# Revit family: Sanitary_Showers_Mincey-Marble_Mincey-Hinged-Door
name_source: partatom
category: Doors
units: mm (PartAtom-declared; Revit-internal decimal feet)

## family parameters
Always vertical = Yes
Cut with Voids When Loaded = No
OmniClass Number = 23.45.05.14.11.24
OmniClass Title = Shower/Bath Screens, Curtains
Room Calculation Point = No
Shared = No
Work Plane-Based = No

## types (9) — shared parameters
Default Elevation = 0"
Description = Frameless Swing
Door Width Note = Available custom sizes. Please, contact the manufacturer.
Glass Material = Mincey Marble Manufacturing - Glass - Clear
Glass Material Note = Available glass type: Clear, Frosted
Height = 96"
Height Note = Available custom sizes. Please, contact the manufacturer.
Hinged Panel Height = 74 9/16"
Hinged Panel Width = 28"
Manufacturer = Mincey Marble Manufacturing
Product Documentation Link = https://minceymarble.com
Product Material = Mincey Marble Manufacturing - Metal - Polished
Product Material Note = Available finishes: Polished, Brushed, Black Matte
Product Page URL = https://minceymarble.com
Radius = 27 3/8"
Rough Height = 96"
Thickness = 5/8"
URL = https://minceymarble.com
Version = 1
zDoor Width 1 = 28"
zDoor Width 2 = 27 1/2"
zHeight = 96"

## per-type parameters (varying)
| type | Fixed Panel Width | Rough Width | Width | zWidth |
| MINHGD - 36 X 96 | 8" | 36" | 36" | 36" |
| MINHGD - 42 X 96 | 14" | 42" | 42" | 42" |
| MINHGD - 48 X 96 | 20" | 48" | 48" | 48" |
| MINHGD - 54 X 96 | 26" | 54" | 54" | 54" |
| MINHGD - 60 X 96 | 32" | 60" | 60" | 60" |
| MINHGD - 66 X 96 | 38" | 66" | 66" | 66" |
| MINHGD - 72 X 96 | 44" | 72" | 72" | 72" |
| MINHGD - 40 X 96 | 12" | 40" | 40" | 40" |
| MINHGD - 46 X 96 | 18" | 46" | 46" | 46" |

note: column(s) folded — value = type name in every type: Model

## geometry (parser evidence)
native form markers: Sweep x3
no freeform markers — native parametric forms only
